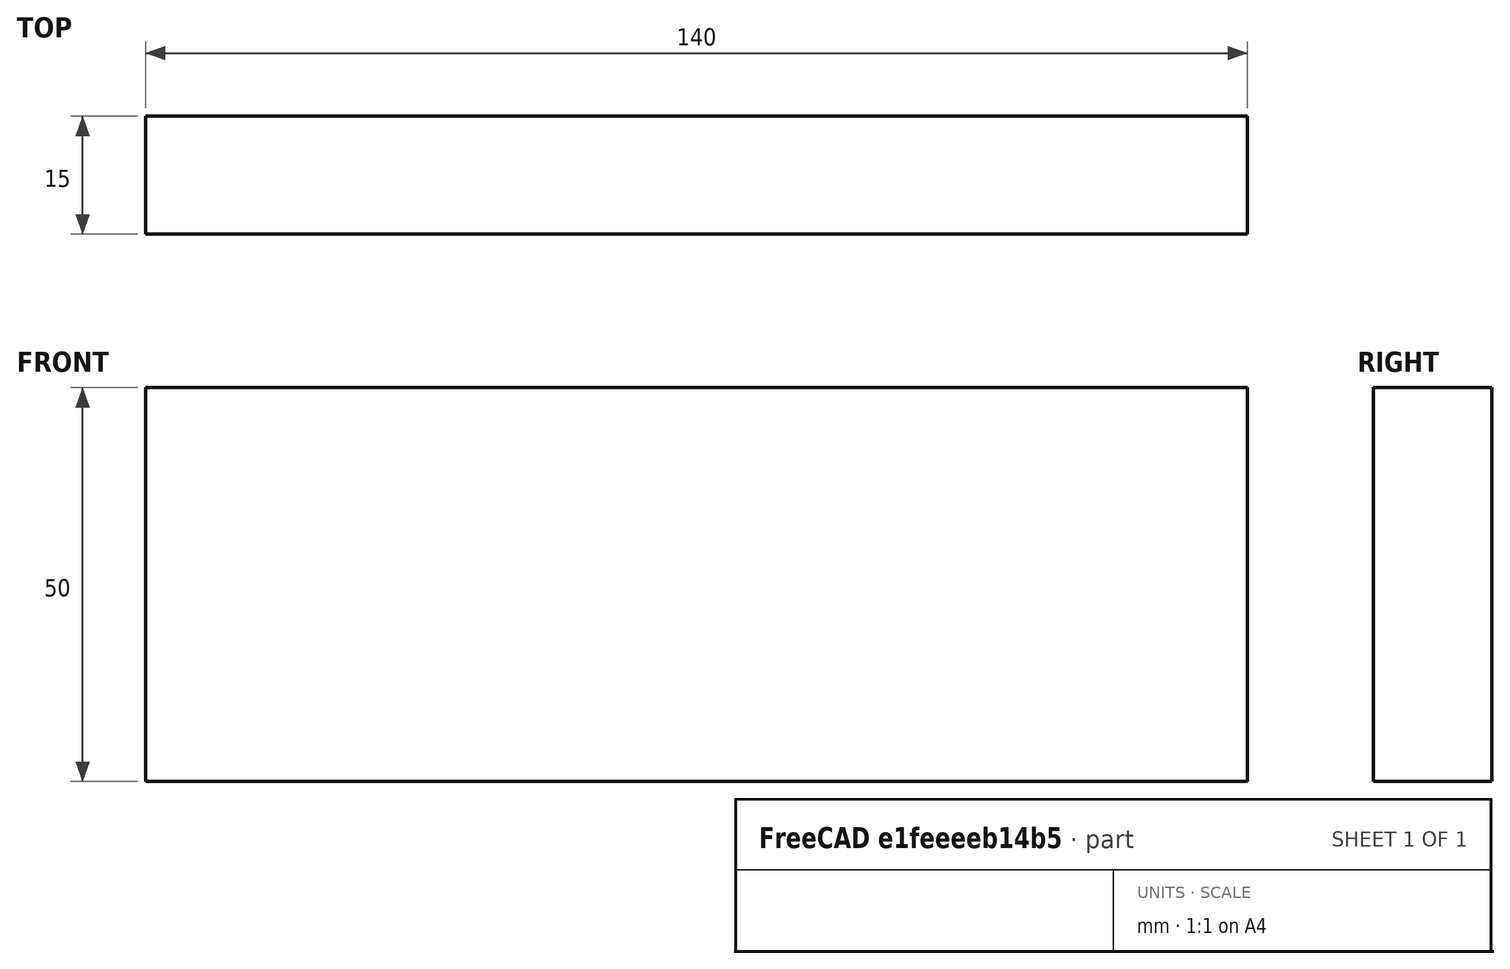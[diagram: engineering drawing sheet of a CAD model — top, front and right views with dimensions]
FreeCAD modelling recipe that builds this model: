
FCSTD DOCUMENT  (FreeCAD 0.15R4671 (Git))
Label: Flat Bar 140x15 EN10058 S235JR
License: All rights reserved
LicenseURL: http://en.wikipedia.org/wiki/All_rights_reserved
objects: Sketcher::SketchObject×1, Part::Extrusion×1
note: 2 computed .brp shape members not serialized (recipe doc carries the construction recipe); baked Part::Feature solids carry a one-line shape summary decoded from their .brp

FEATURE [Sketcher::SketchObject] Sketch
  sketch-geometry (4):
    g0: LineSegment StartX=-70 StartY=-7.5 StartZ=0 EndX=70 EndY=-7.5 EndZ=0
    g1: LineSegment StartX=70 StartY=-7.5 StartZ=0 EndX=70 EndY=7.5 EndZ=0
    g2: LineSegment StartX=70 StartY=7.5 StartZ=0 EndX=-70 EndY=7.5 EndZ=0
    g3: LineSegment StartX=-70 StartY=7.5 StartZ=0 EndX=-70 EndY=-7.5 EndZ=0
  constraints (12):
    c: Coincident(g0,g1)
    c: Coincident(g1,g2)
    c: Coincident(g2,g3)
    c: Coincident(g3,g0)
    c: Horizontal(g0)
    c: Horizontal(g2)
    c: Vertical(g1)
    c: Vertical(g3)
    c: Symmetric(g1,g2,g-2)
    c: Symmetric(g0,g1,g-1)
    c: DistanceY(g1) = 15
    c: DistanceX(g0) = 140
FEATURE [Part::Extrusion] Extrude  label="Flat Bar 140x15 EN10058 S235JR"
  Base = -> Sketch
  Dir = (0,0,50)
  Solid = true
